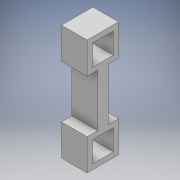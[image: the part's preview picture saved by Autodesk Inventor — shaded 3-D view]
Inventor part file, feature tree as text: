
AUTODESK INVENTOR PART (.ipt)
format: ipt  version: 2018 (Build 220112000, 112)  size: 122,880 bytes
history: native  units: mm
features: sketch x2, extrude x1
ambient origin geometry x8: Origin, YZ Plane, XZ Plane, XY Plane, X Axis, Y Axis, Z Axis, Center Point
bodies: Solid1 (feature_tree)
feature tree (3):
  sketch  "Sketch1"  dims[d0=100.0mm d1=20.0mm]
  extrude  "Extrusion1"  Depth=20.0mm
  sketch  "Sketch2"  dims[d2=60.0mm d3=60.0mm d4=0.0mm d5=20.0mm d6=60.0mm d7=40.0mm d8=40.0mm d9=10.0mm d10=10.0mm d11=40.0mm d12=40.0mm d13=10.0mm d14=10.0mm d15=49.0mm d16=0.0mm]
